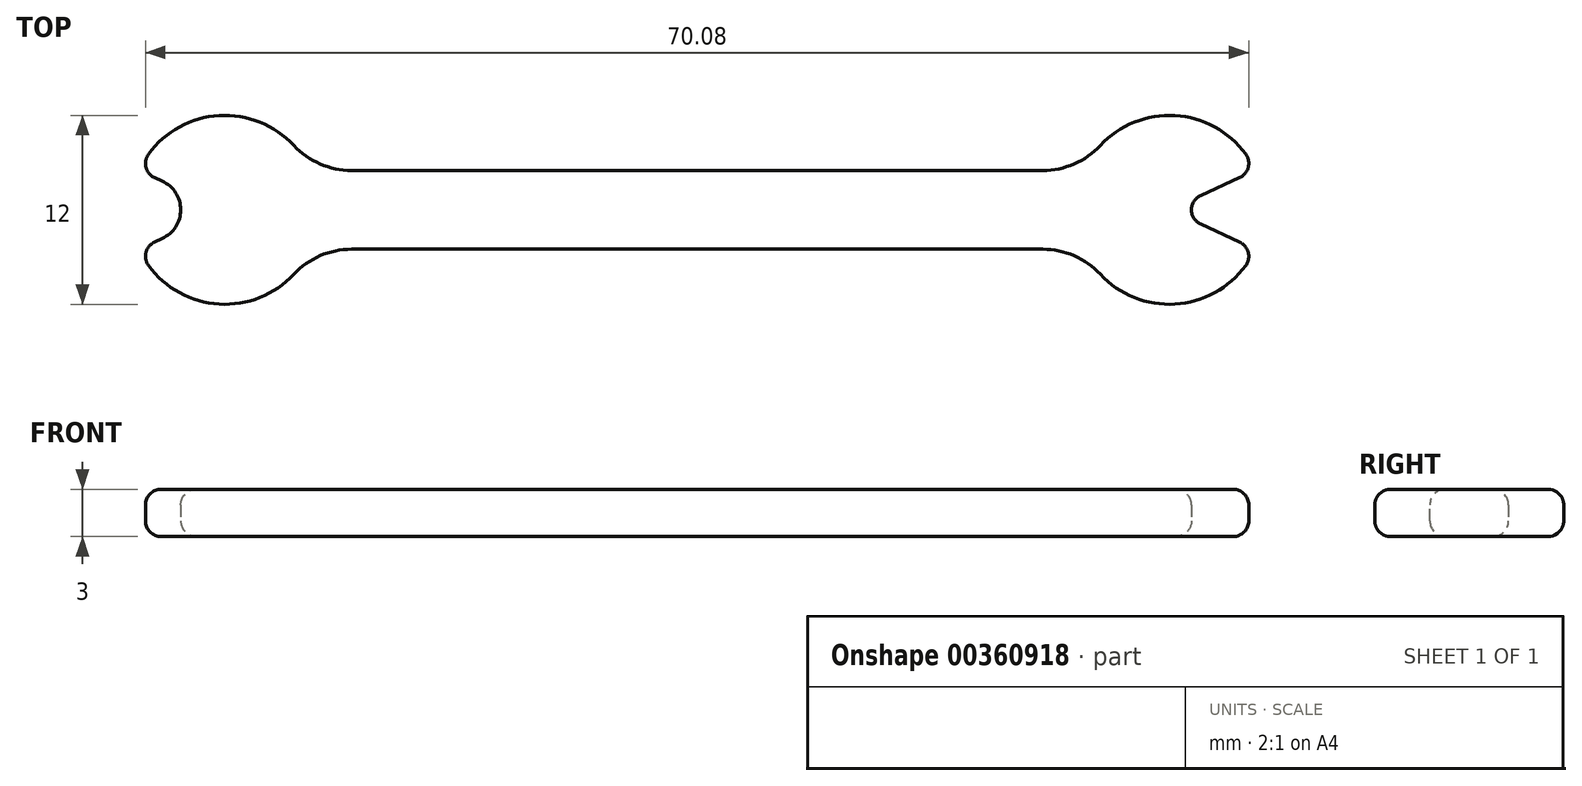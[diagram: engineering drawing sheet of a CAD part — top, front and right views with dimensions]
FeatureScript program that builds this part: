
annotation { "Feature Type Name" : "Feature", "Feature Type Description" : "" }
export const myFeature = defineFeature(function(context is Context, id is Id, definition is map)
    precondition{}
    {
        {
            var Q0;
            Q0=qCreatedBy(makeId("Top.planeOp"),FACE);
            var sketch = newSketch(context, id + "F0", { "sketchPlane" : qUnion([Q0])});
            skLineSegment(sketch, "E0.bottom", {"start": v(0, 0) * mm, "end": v(60, 0) * mm});
            skLineSegment(sketch, "E0.top", {"start": v(0, 5) * mm, "end": v(60, 5) * mm});
            skLineSegment(sketch, "E0.left", {"start": v(0, 0) * mm, "end": v(0, 5) * mm});
            skLineSegment(sketch, "E0.right", {"start": v(60, 0) * mm, "end": v(60, 5) * mm});
            skArc(sketch, "E1", {"start": v(65.45, 5) * mm, "mid": v(54, 2.5) * mm, "end": v(65.45, 0) * mm});
            skArc(sketch, "E2", {"start": v(-5.45, 0) * mm, "mid": v(6, 2.5) * mm, "end": v(-5.45, 5) * mm});
            skLineSegment(sketch, "E3", {"start": v(0, 5) * mm, "end": v(-5.45, 5) * mm});
            skLineSegment(sketch, "E4", {"start": v(0, 0) * mm, "end": v(-5.45, 0) * mm});
            skLineSegment(sketch, "E5", {"start": v(-5.45, 5) * mm, "end": v(-3.97, 4.32) * mm});
            skLineSegment(sketch, "E6", {"start": v(-5.45, 0) * mm, "end": v(-3.97, 0.68) * mm});
            skArc(sketch, "E7.filletArc", {"start": v(-3.97, 0.68) * mm, "mid": v(-2.8, 2.5) * mm, "end": v(-3.97, 4.32) * mm});
            skLineSegment(sketch, "E8", {"start": v(60, 5) * mm, "end": v(65.45, 5) * mm});
            skLineSegment(sketch, "E9", {"start": v(60, 0) * mm, "end": v(65.45, 0) * mm});
            skLineSegment(sketch, "E10", {"start": v(65.45, 0) * mm, "end": v(60, 2.5) * mm});
            skLineSegment(sketch, "E11", {"start": v(65.45, 5) * mm, "end": v(60, 2.5) * mm});
            skArc(sketch, "E12", {"start": v(61.98, 3.4) * mm, "mid": v(61.4, 2.5) * mm, "end": v(61.98, 1.6) * mm});
            skSolve(sketch);
        }
        {
            var Q0;
            Q0 = qSketchRegion(id + "F0", true);
            var Q1;
            {var subQ0=sQuery(id+"F0.wireOp",EDGE,"E0.left");Q1=makeQuery(id+"F0.imprint","IMPRINT",FACE,{"disambiguationData":[TD([[makeQuery(id+"F0.imprint","IMPRINT",EDGE,{"derivedFrom":subQ0}),-1.0]])]});}
            extrude(context, id + "F1", {"entities" : qUnion([Q0, Q1]), "depth" : 3 * mm});
        }
        {
            var Q0;
            Q0=makeQuery(id+"F1.opExtrude","SWEPT_EDGE",EDGE,{"disambiguationData":[OSD([sQuery(id+"F0.wireOp",EDGE,"E0.bottom"),sQuery(id+"F0.wireOp",EDGE,"E2")])]});
            var Q1;
            Q1=makeQuery(id+"F1.opExtrude","SWEPT_EDGE",EDGE,{"disambiguationData":[OSD([sQuery(id+"F0.wireOp",EDGE,"E0.bottom"),sQuery(id+"F0.wireOp",EDGE,"E1")])]});
            var Q2;
            Q2=makeQuery(id+"F1.opExtrude","SWEPT_EDGE",EDGE,{"disambiguationData":[OSD([sQuery(id+"F0.wireOp",EDGE,"E0.top"),sQuery(id+"F0.wireOp",EDGE,"E1")])]});
            var Q3;
            Q3=makeQuery(id+"F1.opExtrude","SWEPT_EDGE",EDGE,{"disambiguationData":[OSD([sQuery(id+"F0.wireOp",EDGE,"E0.top"),sQuery(id+"F0.wireOp",EDGE,"E2")])]});
            fillet(context, id + "F2", {"entities" : qUnion([Q0, Q1, Q2, Q3]), "radius" : 5 * mm, "tangentPropagation" : true, "allowEdgeOverflow" : false});
        }
        {
            var Q0;
            Q0=makeQuery(id+"F1.opExtrude","CAP_FACE",FACE,{"disambiguationData":[OSD([sQuery(id+"F0.wireOp",EDGE,"E0.bottom"),sQuery(id+"F0.wireOp",EDGE,"E0.top"),sQuery(id+"F0.wireOp",EDGE,"E1"),sQuery(id+"F0.wireOp",EDGE,"E2"),sQuery(id+"F0.wireOp",EDGE,"E5"),sQuery(id+"F0.wireOp",EDGE,"E6"),sQuery(id+"F0.wireOp",EDGE,"E7.filletArc"),sQuery(id+"F0.wireOp",EDGE,"E10"),sQuery(id+"F0.wireOp",EDGE,"E11"),sQuery(id+"F0.wireOp",EDGE,"E12")])],"isStart":false});
            var Q1;
            Q1=makeQuery(id+"F1.opExtrude","CAP_FACE",FACE,{"disambiguationData":[OSD([sQuery(id+"F0.wireOp",EDGE,"E0.bottom"),sQuery(id+"F0.wireOp",EDGE,"E0.top"),sQuery(id+"F0.wireOp",EDGE,"E1"),sQuery(id+"F0.wireOp",EDGE,"E2"),sQuery(id+"F0.wireOp",EDGE,"E5"),sQuery(id+"F0.wireOp",EDGE,"E6"),sQuery(id+"F0.wireOp",EDGE,"E7.filletArc"),sQuery(id+"F0.wireOp",EDGE,"E10"),sQuery(id+"F0.wireOp",EDGE,"E11"),sQuery(id+"F0.wireOp",EDGE,"E12")])],"isStart":true});
            var Q2;
            Q2=makeQuery(id+"F1.opExtrude","SWEPT_EDGE",EDGE,{"disambiguationData":[OSD([sQuery(id+"F0.wireOp",EDGE,"E1"),sQuery(id+"F0.wireOp",EDGE,"E9"),sQuery(id+"F0.wireOp",EDGE,"E10")])]});
            var Q3;
            Q3=makeQuery(id+"F1.opExtrude","SWEPT_EDGE",EDGE,{"disambiguationData":[OSD([sQuery(id+"F0.wireOp",EDGE,"E1"),sQuery(id+"F0.wireOp",EDGE,"E8"),sQuery(id+"F0.wireOp",EDGE,"E11")])]});
            var Q4;
            Q4=makeQuery(id+"F1.opExtrude","SWEPT_EDGE",EDGE,{"disambiguationData":[OSD([sQuery(id+"F0.wireOp",EDGE,"E2"),sQuery(id+"F0.wireOp",EDGE,"E4"),sQuery(id+"F0.wireOp",EDGE,"E6")])]});
            var Q5;
            Q5=makeQuery(id+"F1.opExtrude","SWEPT_EDGE",EDGE,{"disambiguationData":[OSD([sQuery(id+"F0.wireOp",EDGE,"E2"),sQuery(id+"F0.wireOp",EDGE,"E3"),sQuery(id+"F0.wireOp",EDGE,"E5")])]});
            fillet(context, id + "F3", {"entities" : qUnion([Q0, Q1, Q2, Q3, Q4, Q5]), "radius" : 1 * mm, "tangentPropagation" : true, "allowEdgeOverflow" : false});
        }
    });
